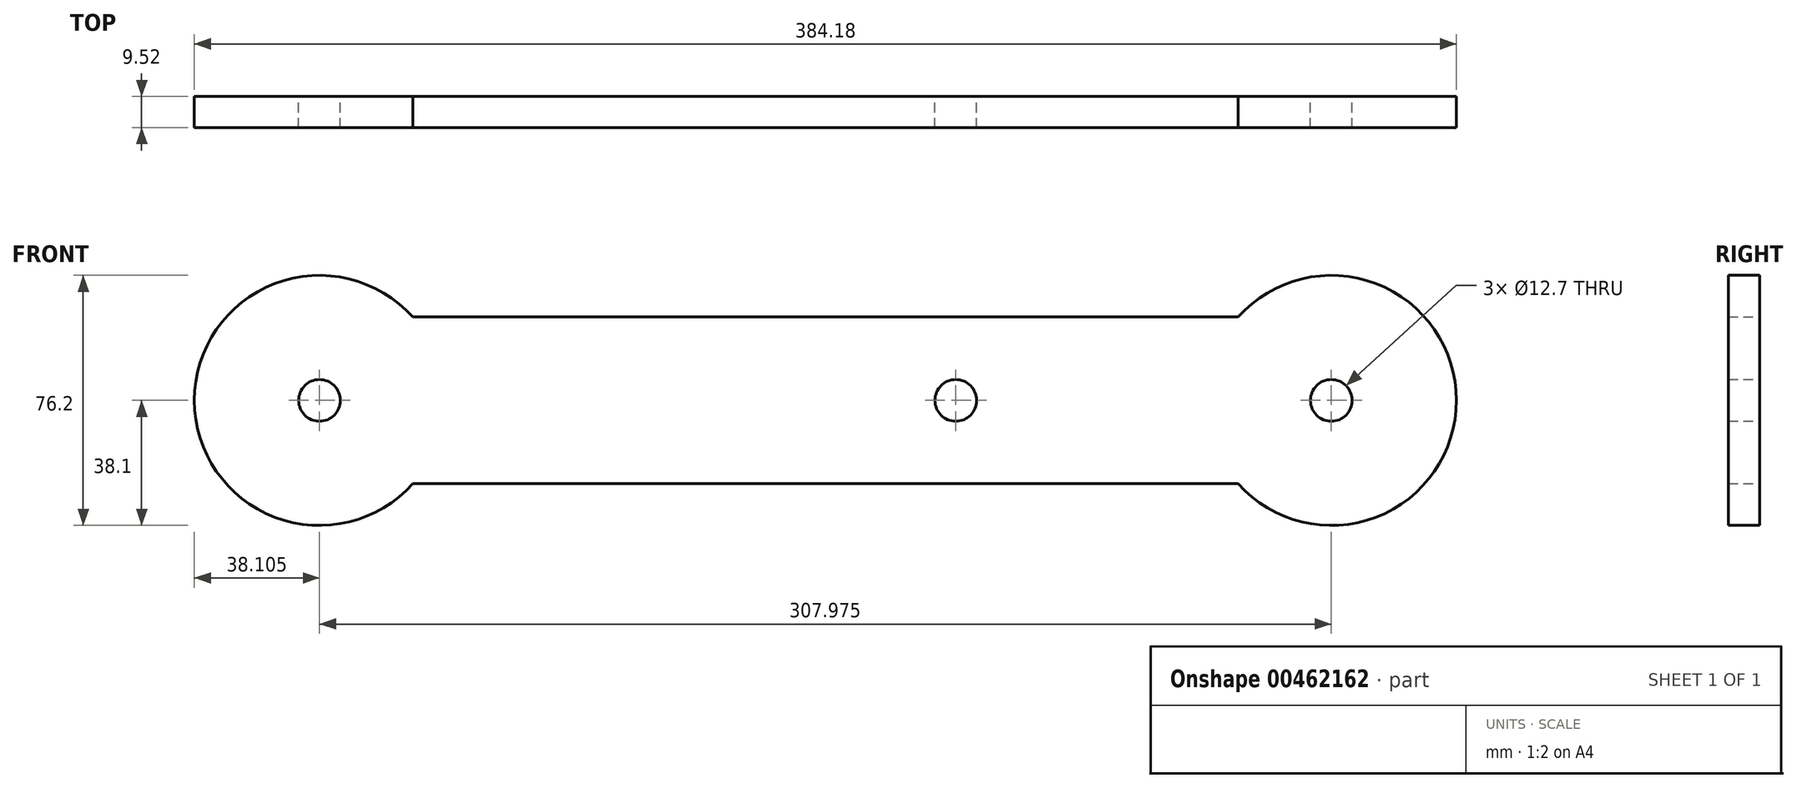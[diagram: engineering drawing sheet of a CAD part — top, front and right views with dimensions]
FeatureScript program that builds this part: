
annotation { "Feature Type Name" : "Feature", "Feature Type Description" : "" }
export const myFeature = defineFeature(function(context is Context, id is Id, definition is map)
    precondition{}
    {
        {
            var Q0;
            Q0=qCreatedBy(makeId("Front.planeOp"),FACE);
            var sketch = newSketch(context, id + "F0", { "sketchPlane" : qUnion([Q0])});
            skLineSegment(sketch, "E0.bottom", {"start": v(203.2, -25.4) * mm, "end": v(-203.2, -25.4) * mm});
            skLineSegment(sketch, "E0.top", {"start": v(203.2, 25.4) * mm, "end": v(-203.2, 25.4) * mm});
            skLineSegment(sketch, "E0.left", {"start": v(203.2, -25.4) * mm, "end": v(203.2, 25.4) * mm});
            skLineSegment(sketch, "E0.right", {"start": v(-203.2, -25.4) * mm, "end": v(-203.2, 25.4) * mm});
            skPoint(sketch, "E0.middle", {"position": v(0, 0) * mm});
            skLineSegment(sketch, "E1", {"start": v(203.2, 0) * mm, "end": v(-203.2, 0) * mm, "construction": true});
            skPoint(sketch, "E2", {"position": v(-168.28, 0) * mm});
            skPoint(sketch, "E3", {"position": v(-130.18, 0) * mm});
            skPoint(sketch, "E4", {"position": v(177.8, 0) * mm});
            skCircle(sketch, "E5", {"center": v(-130.18, 0) * mm, "radius": 25.4 * mm});
            skCircle(sketch, "E6", {"center": v(-130.18, 0) * mm, "radius": 6.35 * mm});
            skCircle(sketch, "E7", {"center": v(177.8, 0) * mm, "radius": 6.35 * mm});
            skCircle(sketch, "E8", {"center": v(-130.18, 0) * mm, "radius": 38.1 * mm});
            skCircle(sketch, "E9", {"center": v(177.8, 0) * mm, "radius": 38.1 * mm});
            skCircle(sketch, "E10", {"center": v(63.5, 0) * mm, "radius": 6.35 * mm});
            skSolve(sketch);
        }
        {
            var Q0;
            {var subQ0=sQuery(id+"F0.wireOp",EDGE,"E9");var subQ1=sQuery(id+"F0.wireOp",EDGE,"E0.bottom");var subQ2=makeQuery(id+"F0.imprint","INTERSECT",VERTEX,{"derivedFrom":[subQ1,subQ0]});Q0=makeQuery(id+"F0.imprint","IMPRINT",FACE,{"disambiguationData":[TD([[makeQuery(id+"F0.imprint","IMPRINT",EDGE,{"disambiguationData":[TD([[subQ2,-1.0]])],"derivedFrom":subQ1}),-1.0]])]});}
            var Q1;
            {var subQ0=sQuery(id+"F0.wireOp",EDGE,"E8");var subQ1=sQuery(id+"F0.wireOp",EDGE,"E0.bottom");var subQ2=makeQuery(id+"F0.imprint","INTERSECT",VERTEX,{"disambiguationData":[OD(0.0)],"derivedFrom":[subQ1,subQ0]});Q1=makeQuery(id+"F0.imprint","IMPRINT",FACE,{"disambiguationData":[TD([[makeQuery(id+"F0.imprint","IMPRINT",EDGE,{"disambiguationData":[TD([[subQ2,-1.0]])],"derivedFrom":subQ1}),-1.0]])]});}
            var Q2;
            Q2=makeQuery(id+"F0.imprint","IMPRINT",FACE,{"disambiguationData":[TD([[makeQuery(id+"F0.imprint","IMPRINT",EDGE,{"derivedFrom":sQuery(id+"F0.wireOp",EDGE,"E6")}),-1.0]])]});
            var Q3;
            {var subQ0=sQuery(id+"F0.wireOp",EDGE,"E8");var subQ1=sQuery(id+"F0.wireOp",EDGE,"E0.top");var subQ2=makeQuery(id+"F0.imprint","INTERSECT",VERTEX,{"disambiguationData":[OD(0.0)],"derivedFrom":[subQ1,subQ0]});Q3=makeQuery(id+"F0.imprint","IMPRINT",FACE,{"disambiguationData":[TD([[makeQuery(id+"F0.imprint","IMPRINT",EDGE,{"disambiguationData":[TD([[subQ2,-1.0]])],"derivedFrom":subQ1}),-1.0]])]});}
            var Q4;
            {var subQ0=sQuery(id+"F0.wireOp",EDGE,"E8");var subQ1=sQuery(id+"F0.wireOp",EDGE,"E0.bottom");var subQ2=makeQuery(id+"F0.imprint","INTERSECT",VERTEX,{"disambiguationData":[OD(1.0)],"derivedFrom":[subQ1,subQ0]});Q4=makeQuery(id+"F0.imprint","IMPRINT",FACE,{"disambiguationData":[TD([[makeQuery(id+"F0.imprint","IMPRINT",EDGE,{"disambiguationData":[TD([[subQ2,1.0]])],"derivedFrom":subQ1}),-1.0]])]});}
            var Q5;
            {var subQ0=sQuery(id+"F0.wireOp",EDGE,"E8");var subQ1=sQuery(id+"F0.wireOp",EDGE,"E0.bottom");var subQ2=makeQuery(id+"F0.imprint","INTERSECT",VERTEX,{"disambiguationData":[OD(0.0)],"derivedFrom":[subQ1,subQ0]});Q5=makeQuery(id+"F0.imprint","IMPRINT",FACE,{"disambiguationData":[TD([[makeQuery(id+"F0.imprint","IMPRINT",EDGE,{"disambiguationData":[TD([[subQ2,-1.0]])],"derivedFrom":subQ1}),1.0]])]});}
            var Q6;
            {var subQ0=sQuery(id+"F0.wireOp",EDGE,"E0.left");Q6=makeQuery(id+"F0.imprint","IMPRINT",FACE,{"disambiguationData":[TD([[makeQuery(id+"F0.imprint","IMPRINT",EDGE,{"derivedFrom":subQ0}),-1.0]])]});}
            var Q7;
            {var subQ0=sQuery(id+"F0.wireOp",EDGE,"E0.left");Q7=makeQuery(id+"F0.imprint","IMPRINT",FACE,{"disambiguationData":[TD([[makeQuery(id+"F0.imprint","IMPRINT",EDGE,{"derivedFrom":subQ0}),1.0]])]});}
            extrude(context, id + "F1", {"entities" : qUnion([Q0, Q1, Q2, Q3, Q4, Q5, Q6, Q7]), "depth" : 9.52 * mm, "symmetric" : true});
        }
    });
